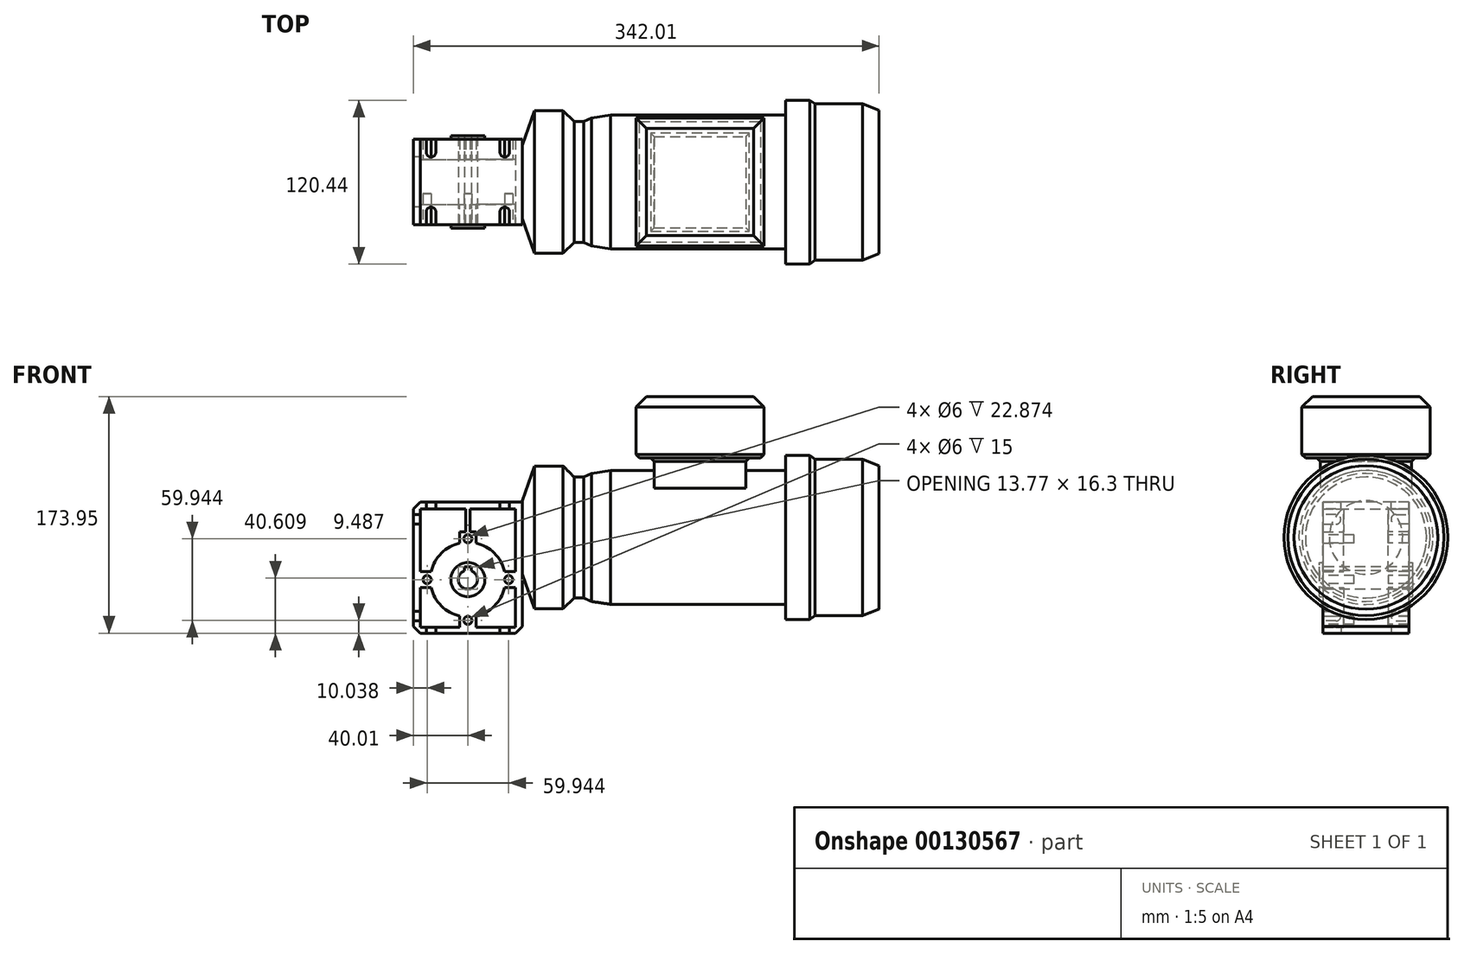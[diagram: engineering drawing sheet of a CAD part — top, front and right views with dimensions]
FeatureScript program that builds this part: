
annotation { "Feature Type Name" : "Feature", "Feature Type Description" : "" }
export const myFeature = defineFeature(function(context is Context, id is Id, definition is map)
    precondition{}
    {
        {
            var Q0;
            Q0=qCreatedBy(makeId("Top.planeOp"),FACE);
            var sketch = newSketch(context, id + "F0", { "sketchPlane" : qUnion([Q0])});
            skLineSegment(sketch, "E0.bottom", {"start": v(-40, 16.5) * mm, "end": v(40, 16.5) * mm});
            skLineSegment(sketch, "E0.top", {"start": v(-40, -16.5) * mm, "end": v(40, -16.5) * mm});
            skLineSegment(sketch, "E0.left", {"start": v(-40, 16.5) * mm, "end": v(-40, -16.5) * mm});
            skLineSegment(sketch, "E0.right", {"start": v(40, 16.5) * mm, "end": v(40, -16.5) * mm});
            skPoint(sketch, "E0.middle", {"position": v(0, 0) * mm});
            skSolve(sketch);
        }
        {
            var Q0;
            Q0=qSketchRegion(id+"F0",true);
            extrude(context, id + "F1", {"entities" : qUnion([Q0]), "endBound" : BoundingType.SYMMETRIC, "depth" : 96.35 * mm});
        }
        {
            var Q0;
            Q0=makeQuery(id+"F1.opExtrude","SWEPT_FACE",FACE,{"disambiguationData":[OSD([sQuery(id+"F0.wireOp",EDGE,"E0.top")])]});
            var sketch = newSketch(context, id + "F2", { "sketchPlane" : qUnion([Q0])});
            skArc(sketch, "E1", {"start": v(-2.5, -2.18) * mm, "mid": v(0, -15.72) * mm, "end": v(2.5, -2.18) * mm});
            skLineSegment(sketch, "E2", {"start": v(-2.5, -2.18) * mm, "end": v(-2.5, 0.58) * mm});
            skLineSegment(sketch, "E3", {"start": v(-2.5, 0.58) * mm, "end": v(2.5, 0.58) * mm});
            skLineSegment(sketch, "E4", {"start": v(2.5, 0.58) * mm, "end": v(2.5, -2.18) * mm});
            skPoint(sketch, "E5", {"position": v(0, -15.72) * mm});
            skSolve(sketch);
        }
        {
            var Q0;
            Q0=qSketchRegion(id+"F2",true);
            extrude(context, id + "F3", {"entities" : qUnion([Q0]), "operationType" : NewBodyOperationType.REMOVE, "endBound" : BoundingType.UP_TO_NEXT, "oppositeDirection" : true, "depth" : 25.4 * mm});
        }
        {
            var Q0;
            Q0=qCreatedBy(makeId("Front.planeOp"),FACE);
            var sketch = newSketch(context, id + "F4", { "sketchPlane" : qUnion([Q0])});
            skCircle(sketch, "E6", {"center": v(0, -8.72) * mm, "radius": 12.5 * mm});
            skArc(sketch, "E7.0", {"start": v(-2.5, -2.18) * mm, "mid": v(0, -15.72) * mm, "end": v(2.5, -2.18) * mm});
            skLineSegment(sketch, "E8.0", {"start": v(2.5, 0.58) * mm, "end": v(2.5, -2.18) * mm});
            skLineSegment(sketch, "E9.0", {"start": v(-2.5, 0.58) * mm, "end": v(2.5, 0.58) * mm});
            skLineSegment(sketch, "E10.0", {"start": v(-2.5, -2.18) * mm, "end": v(-2.5, 0.58) * mm});
            skSolve(sketch);
        }
        {
            var Q0;
            Q0=qSketchRegion(id+"F4",true);
            extrude(context, id + "F5", {"entities" : qUnion([Q0]), "operationType" : NewBodyOperationType.ADD, "endBound" : BoundingType.SYMMETRIC, "depth" : 68.07 * mm});
        }
        {
            var Q0;
            Q0=makeQuery(id+"F1.opExtrude","SWEPT_FACE",FACE,{"disambiguationData":[OSD([sQuery(id+"F0.wireOp",EDGE,"E0.top")])]});
            var sketch = newSketch(context, id + "F6", { "sketchPlane" : qUnion([Q0])});
            skCircle(sketch, "E11", {"center": v(0, 21.25) * mm, "radius": 3 * mm});
            skPoint(sketch, "E12", {"position": v(0, -8.72) * mm});
            skCircle(sketch, "E13.1.0", {"center": v(-29.97, -8.72) * mm, "radius": 3 * mm});
            skCircle(sketch, "E13.2.0", {"center": v(0, -38.7) * mm, "radius": 3 * mm});
            skCircle(sketch, "E13.3.0", {"center": v(29.97, -8.72) * mm, "radius": 3 * mm});
            skSolve(sketch);
        }
        {
            var Q0;
            Q0=qSketchRegion(id+"F6",true);
            extrude(context, id + "F7", {"entities" : qUnion([Q0]), "operationType" : NewBodyOperationType.REMOVE, "oppositeDirection" : true, "depth" : 7.87 * mm});
        }
        {
            var Q0;
            Q0=makeQuery(id+"F1.opExtrude","SWEPT_FACE",FACE,{"disambiguationData":[OSD([sQuery(id+"F0.wireOp",EDGE,"E0.top")])]});
            var sketch = newSketch(context, id + "F8", { "sketchPlane" : qUnion([Q0])});
            skLineSegment(sketch, "E14", {"start": v(-6, 18.12) * mm, "end": v(-6, 26.28) * mm});
            skLineSegment(sketch, "E15", {"start": v(-6, 26.28) * mm, "end": v(6, 26.28) * mm});
            skLineSegment(sketch, "E16", {"start": v(6, 26.28) * mm, "end": v(6, 18.12) * mm});
            skArc(sketch, "E17", {"start": v(-6, 18.12) * mm, "mid": v(-19.45, 10.72) * mm, "end": v(-26.84, -2.72) * mm});
            skArc(sketch, "E18", {"start": v(6, 18.12) * mm, "mid": v(0, 18.78) * mm, "end": v(-6, 18.12) * mm, "construction": true});
            skLineSegment(sketch, "E19", {"start": v(-6, -35.56) * mm, "end": v(-6, -35.56) * mm});
            skLineSegment(sketch, "E20", {"start": v(-6, -43.72) * mm, "end": v(6, -43.72) * mm});
            skLineSegment(sketch, "E21", {"start": v(6, -43.72) * mm, "end": v(6, -35.56) * mm});
            skLineSegment(sketch, "E22", {"start": v(-6, -35.56) * mm, "end": v(-6, -43.72) * mm});
            skArc(sketch, "E23", {"start": v(-6, -35.56) * mm, "mid": v(0, -36.22) * mm, "end": v(6, -35.56) * mm, "construction": true});
            skArc(sketch, "E24", {"start": v(6, -35.56) * mm, "mid": v(19.45, -28.17) * mm, "end": v(26.84, -14.72) * mm});
            skLineSegment(sketch, "E25", {"start": v(-35, -2.72) * mm, "end": v(-35, -14.72) * mm});
            skLineSegment(sketch, "E26", {"start": v(-35, -14.72) * mm, "end": v(-26.84, -14.72) * mm});
            skLineSegment(sketch, "E27", {"start": v(26.84, -2.72) * mm, "end": v(35, -2.72) * mm});
            skLineSegment(sketch, "E28", {"start": v(35, -2.72) * mm, "end": v(35, -14.72) * mm});
            skLineSegment(sketch, "E29", {"start": v(35, -14.72) * mm, "end": v(26.84, -14.72) * mm});
            skLineSegment(sketch, "E30", {"start": v(-35, -2.72) * mm, "end": v(-26.84, -2.72) * mm});
            skArc(sketch, "E31", {"start": v(-26.84, -2.72) * mm, "mid": v(-27.5, -8.72) * mm, "end": v(-26.84, -14.72) * mm, "construction": true});
            skArc(sketch, "E32", {"start": v(-26.84, -14.72) * mm, "mid": v(-19.45, -28.17) * mm, "end": v(-6, -35.56) * mm});
            skArc(sketch, "E33", {"start": v(26.84, -14.72) * mm, "mid": v(27.5, -8.72) * mm, "end": v(26.84, -2.72) * mm, "construction": true});
            skArc(sketch, "E34", {"start": v(26.84, -2.72) * mm, "mid": v(19.45, 10.72) * mm, "end": v(6, 18.12) * mm});
            skLineSegment(sketch, "E35", {"start": v(-35, -2.72) * mm, "end": v(-35, 43.17) * mm});
            skLineSegment(sketch, "E36", {"start": v(-35, 43.17) * mm, "end": v(-1.5, 43.17) * mm});
            skLineSegment(sketch, "E37", {"start": v(-1.5, 43.17) * mm, "end": v(-1.5, 26.28) * mm});
            skLineSegment(sketch, "E38", {"start": v(1.5, 26.28) * mm, "end": v(1.5, 43.17) * mm});
            skLineSegment(sketch, "E39", {"start": v(1.5, 43.17) * mm, "end": v(35, 43.17) * mm});
            skLineSegment(sketch, "E40", {"start": v(35, 43.17) * mm, "end": v(35, -2.72) * mm});
            skLineSegment(sketch, "E41", {"start": v(35, -14.72) * mm, "end": v(35, -43.72) * mm});
            skLineSegment(sketch, "E42", {"start": v(35, -43.72) * mm, "end": v(6, -43.72) * mm});
            skLineSegment(sketch, "E43", {"start": v(-35, -14.72) * mm, "end": v(-35, -43.72) * mm});
            skLineSegment(sketch, "E44", {"start": v(-35, -43.72) * mm, "end": v(-6, -43.72) * mm});
            skLineSegment(sketch, "E45", {"start": v(-35, 43.17) * mm, "end": v(-40, 43.17) * mm, "construction": true});
            skLineSegment(sketch, "E46", {"start": v(-35, 43.17) * mm, "end": v(-35, 48.17) * mm, "construction": true});
            skSolve(sketch);
        }
        {
            var Q0;
            Q0=makeQuery(id+"F8.imprint","IMPRINT",FACE,{"disambiguationData":[TD([[makeQuery(id+"F8.imprint","IMPRINT",EDGE,{"derivedFrom":sQuery(id+"F8.wireOp",EDGE,"E20")}),-1.0]])]});
            var Q1;
            {var subQ4=sQuery(id+"F8.wireOp",EDGE,"E14");Q1=makeQuery(id+"F8.imprint","IMPRINT",FACE,{"disambiguationData":[TD([[makeQuery(id+"F8.imprint","IMPRINT",EDGE,{"derivedFrom":subQ4}),-1.0]])]});}
            extrude(context, id + "F9", {"entities" : qUnion([Q0, Q1]), "depth" : 15 * mm});
        }
        {
            var Q0;
            Q0=makeQuery(id+"F9.opExtrude","SWEPT_BODY",BODY,{"disambiguationData":[OSD([sQuery(id+"F0.wireOp",EDGE,"E0.top"),sQuery(id+"F0.wireOp",EDGE,"E0.left"),sQuery(id+"F0.wireOp",EDGE,"E0.right"),sQuery(id+"F4.wireOp",EDGE,"E6"),sQuery(id+"F6.wireOp",EDGE,"E11"),sQuery(id+"F6.wireOp",EDGE,"E13.1.0"),sQuery(id+"F6.wireOp",EDGE,"E13.2.0"),sQuery(id+"F6.wireOp",EDGE,"E13.3.0"),sQuery(id+"F8.wireOp",EDGE,"E14"),sQuery(id+"F8.wireOp",EDGE,"E15"),sQuery(id+"F8.wireOp",EDGE,"E16"),sQuery(id+"F8.wireOp",EDGE,"E17"),sQuery(id+"F8.wireOp",EDGE,"E21"),sQuery(id+"F8.wireOp",EDGE,"E22"),sQuery(id+"F8.wireOp",EDGE,"E24"),sQuery(id+"F8.wireOp",EDGE,"E26"),sQuery(id+"F8.wireOp",EDGE,"E27"),sQuery(id+"F8.wireOp",EDGE,"E29"),sQuery(id+"F8.wireOp",EDGE,"E30"),sQuery(id+"F8.wireOp",EDGE,"E32"),sQuery(id+"F8.wireOp",EDGE,"E34"),sQuery(id+"F8.wireOp",EDGE,"E35"),sQuery(id+"F8.wireOp",EDGE,"E36"),sQuery(id+"F8.wireOp",EDGE,"E37"),sQuery(id+"F8.wireOp",EDGE,"E38"),sQuery(id+"F8.wireOp",EDGE,"E39"),sQuery(id+"F8.wireOp",EDGE,"E40"),sQuery(id+"F8.wireOp",EDGE,"E41"),sQuery(id+"F8.wireOp",EDGE,"E42"),sQuery(id+"F8.wireOp",EDGE,"E43"),sQuery(id+"F8.wireOp",EDGE,"E44")])]});
            var Q1;
            Q1=qCreatedBy(makeId("Front.planeOp"),FACE);
            mirror(context, id + "F10", {"operationType" : NewBodyOperationType.ADD, "entities" : qUnion([Q0]), "mirrorPlane" : qUnion([Q1])});
        }
        {
            var Q0;
            {var subQ0=sQuery(id+"F0.wireOp",EDGE,"E0.top");var subQ1=makeQuery(id+"F9.opExtrude","SWEPT_FACE",FACE,{"disambiguationData":[OSD([subQ0]),TDD([makeQuery(id+"F8.imprint","IMPRINT",EDGE,{"derivedFrom":makeQuery(id+"F1.opExtrude","CAP_EDGE",EDGE,{"disambiguationData":[OSD([subQ0])],"isStart":false})})])]});Q0=makeQuery(id+"F10.boolean.opBoolean","MERGE",FACE,{"derivedFrom":[makeQuery(id+"F1.opExtrude","CAP_FACE",FACE,{"disambiguationData":[OSD([sQuery(id+"F0.wireOp",EDGE,"E0.bottom"),subQ0,sQuery(id+"F0.wireOp",EDGE,"E0.left"),sQuery(id+"F0.wireOp",EDGE,"E0.right")])],"isStart":false}),subQ1,makeQuery(id+"F10.opPattern","COPY",FACE,{"derivedFrom":subQ1,"instanceName":"1"})]});}
            var sketch = newSketch(context, id + "F11", { "sketchPlane" : qUnion([Q0])});
            skLineSegment(sketch, "E47", {"start": v(-30.6, -31.5) * mm, "end": v(-30.6, -21.97) * mm});
            skLineSegment(sketch, "E48", {"start": v(-23.5, -31.5) * mm, "end": v(-23.5, -21.97) * mm});
            skArc(sketch, "E49", {"start": v(-30.6, -21.97) * mm, "mid": v(-27.05, -18.41) * mm, "end": v(-23.5, -21.97) * mm});
            skLineSegment(sketch, "E50", {"start": v(-30.6, -31.5) * mm, "end": v(-23.5, -31.5) * mm});
            skArc(sketch, "E51.MirrorCS", {"start": v(30.6, -21.97) * mm, "mid": v(27.05, -18.41) * mm, "end": v(23.5, -21.97) * mm});
            skLineSegment(sketch, "E52.MirrorCS", {"start": v(23.5, -31.5) * mm, "end": v(23.5, -21.97) * mm});
            skLineSegment(sketch, "E53.MirrorCS", {"start": v(30.6, -31.5) * mm, "end": v(30.6, -21.97) * mm});
            skLineSegment(sketch, "E54.MirrorCS", {"start": v(30.6, -31.5) * mm, "end": v(23.5, -31.5) * mm});
            skArc(sketch, "E55.MirrorCS", {"start": v(-30.6, 21.97) * mm, "mid": v(-27.05, 18.41) * mm, "end": v(-23.5, 21.97) * mm});
            skLineSegment(sketch, "E56.MirrorCS", {"start": v(-30.6, 31.5) * mm, "end": v(-30.6, 21.97) * mm});
            skLineSegment(sketch, "E57.MirrorCS", {"start": v(-23.5, 31.5) * mm, "end": v(-23.5, 21.97) * mm});
            skLineSegment(sketch, "E58.MirrorCS", {"start": v(-30.6, 31.5) * mm, "end": v(-23.5, 31.5) * mm});
            skLineSegment(sketch, "E59.MirrorCS", {"start": v(30.6, 31.5) * mm, "end": v(23.5, 31.5) * mm});
            skLineSegment(sketch, "E60.MirrorCS", {"start": v(23.5, 31.5) * mm, "end": v(23.5, 21.97) * mm});
            skArc(sketch, "E61.MirrorCS", {"start": v(30.6, 21.97) * mm, "mid": v(27.05, 18.41) * mm, "end": v(23.5, 21.97) * mm});
            skLineSegment(sketch, "E62.MirrorCS", {"start": v(30.6, 31.5) * mm, "end": v(30.6, 21.97) * mm});
            skSolve(sketch);
        }
        {
            var Q0;
            Q0=qSketchRegion(id+"F11",true);
            extrude(context, id + "F12", {"entities" : qUnion([Q0]), "operationType" : NewBodyOperationType.REMOVE, "endBound" : BoundingType.UP_TO_NEXT, "oppositeDirection" : true, "depth" : 114.3 * mm});
        }
        {
            var Q0;
            {var subQ0=sQuery(id+"F0.wireOp",EDGE,"E0.top");var subQ1=makeQuery(id+"F9.opExtrude","SWEPT_FACE",FACE,{"disambiguationData":[OSD([subQ0]),TDD([makeQuery(id+"F8.imprint","IMPRINT",EDGE,{"derivedFrom":makeQuery(id+"F1.opExtrude","CAP_EDGE",EDGE,{"disambiguationData":[OSD([subQ0])],"isStart":true})})])]});Q0=makeQuery(id+"F10.boolean.opBoolean","MERGE",FACE,{"derivedFrom":[makeQuery(id+"F1.opExtrude","CAP_FACE",FACE,{"disambiguationData":[OSD([sQuery(id+"F0.wireOp",EDGE,"E0.bottom"),subQ0,sQuery(id+"F0.wireOp",EDGE,"E0.left"),sQuery(id+"F0.wireOp",EDGE,"E0.right")])],"isStart":true}),subQ1,makeQuery(id+"F10.opPattern","COPY",FACE,{"derivedFrom":subQ1,"instanceName":"1"})]});}
            var sketch = newSketch(context, id + "F13", { "sketchPlane" : qUnion([Q0])});
            skLineSegment(sketch, "E63.0", {"start": v(-23.5, 21.97) * mm, "end": v(-23.5, 31.5) * mm});
            skArc(sketch, "E64.0", {"start": v(-23.5, 21.97) * mm, "mid": v(-27.05, 18.41) * mm, "end": v(-30.6, 21.97) * mm});
            skLineSegment(sketch, "E65.0", {"start": v(-30.6, 21.97) * mm, "end": v(-30.6, 31.5) * mm});
            skLineSegment(sketch, "E66.0", {"start": v(23.5, 21.97) * mm, "end": v(23.5, 31.5) * mm});
            skArc(sketch, "E67.0", {"start": v(23.5, 21.97) * mm, "mid": v(27.05, 18.41) * mm, "end": v(30.6, 21.97) * mm});
            skLineSegment(sketch, "E68.0", {"start": v(30.6, 21.97) * mm, "end": v(30.6, 31.5) * mm});
            skLineSegment(sketch, "E69", {"start": v(-30.6, 31.5) * mm, "end": v(-23.5, 31.5) * mm});
            skLineSegment(sketch, "E70", {"start": v(23.5, 31.5) * mm, "end": v(30.6, 31.5) * mm});
            skLineSegment(sketch, "E71.MirrorCS", {"start": v(23.5, -21.97) * mm, "end": v(23.5, -31.5) * mm});
            skArc(sketch, "E72.MirrorCS", {"start": v(23.5, -21.97) * mm, "mid": v(27.05, -18.41) * mm, "end": v(30.6, -21.97) * mm});
            skLineSegment(sketch, "E73.MirrorCS", {"start": v(30.6, -21.97) * mm, "end": v(30.6, -31.5) * mm});
            skLineSegment(sketch, "E74.MirrorCS", {"start": v(23.5, -31.5) * mm, "end": v(30.6, -31.5) * mm});
            skLineSegment(sketch, "E75.MirrorCS", {"start": v(-30.6, -31.5) * mm, "end": v(-23.5, -31.5) * mm});
            skLineSegment(sketch, "E76.MirrorCS", {"start": v(-30.6, -21.97) * mm, "end": v(-30.6, -31.5) * mm});
            skArc(sketch, "E77.MirrorCS", {"start": v(-23.5, -21.97) * mm, "mid": v(-27.05, -18.41) * mm, "end": v(-30.6, -21.97) * mm});
            skLineSegment(sketch, "E78.MirrorCS", {"start": v(-23.5, -21.97) * mm, "end": v(-23.5, -31.5) * mm});
            skSolve(sketch);
        }
        {
            var Q0;
            Q0=qSketchRegion(id+"F13",true);
            extrude(context, id + "F14", {"entities" : qUnion([Q0]), "operationType" : NewBodyOperationType.REMOVE, "endBound" : BoundingType.UP_TO_NEXT, "oppositeDirection" : true, "depth" : 25.4 * mm});
        }
        {
            var Q0;
            {var subQ0=sQuery(id+"F0.wireOp",EDGE,"E0.left");var subQ1=makeQuery(id+"F9.opExtrude","SWEPT_FACE",FACE,{"disambiguationData":[OSD([sQuery(id+"F0.wireOp",EDGE,"E0.top"),subQ0])]});Q0=makeQuery(id+"F10.boolean.opBoolean","MERGE",FACE,{"derivedFrom":[makeQuery(id+"F1.opExtrude","SWEPT_FACE",FACE,{"disambiguationData":[OSD([subQ0])]}),subQ1,makeQuery(id+"F10.opPattern","COPY",FACE,{"derivedFrom":subQ1,"instanceName":"1"})]});}
            var sketch = newSketch(context, id + "F15", { "sketchPlane" : qUnion([Q0])});
            skLineSegment(sketch, "E79", {"start": v(31.5, 39.12) * mm, "end": v(31.5, 32) * mm});
            skArc(sketch, "E80.MirrorCS", {"start": v(21.97, 39.12) * mm, "mid": v(18.42, 35.56) * mm, "end": v(21.97, 32) * mm});
            skLineSegment(sketch, "E81", {"start": v(21.97, 39.12) * mm, "end": v(31.5, 39.12) * mm});
            skLineSegment(sketch, "E82", {"start": v(31.5, 32) * mm, "end": v(21.97, 32) * mm});
            skArc(sketch, "E83.MirrorCS", {"start": v(-21.97, 39.12) * mm, "mid": v(-18.41, 35.56) * mm, "end": v(-21.97, 32) * mm});
            skLineSegment(sketch, "E84.MirrorCS", {"start": v(-21.97, 39.12) * mm, "end": v(-31.5, 39.12) * mm});
            skLineSegment(sketch, "E85.MirrorCS", {"start": v(-31.5, 32) * mm, "end": v(-21.97, 32) * mm});
            skLineSegment(sketch, "E86.MirrorCS", {"start": v(-31.5, 39.12) * mm, "end": v(-31.5, 32) * mm});
            skLineSegment(sketch, "E87.MirrorCS", {"start": v(-31.5, -39.12) * mm, "end": v(-31.5, -32) * mm});
            skLineSegment(sketch, "E88.MirrorCS", {"start": v(-31.5, -32) * mm, "end": v(-21.97, -32) * mm});
            skArc(sketch, "E89.MirrorCS", {"start": v(-21.97, -39.12) * mm, "mid": v(-18.41, -35.56) * mm, "end": v(-21.97, -32) * mm});
            skLineSegment(sketch, "E90.MirrorCS", {"start": v(-21.97, -39.12) * mm, "end": v(-31.5, -39.12) * mm});
            skArc(sketch, "E91.MirrorCS", {"start": v(21.97, -39.12) * mm, "mid": v(18.42, -35.56) * mm, "end": v(21.97, -32) * mm});
            skLineSegment(sketch, "E92.MirrorCS", {"start": v(31.5, -32) * mm, "end": v(21.97, -32) * mm});
            skLineSegment(sketch, "E93.MirrorCS", {"start": v(31.5, -39.12) * mm, "end": v(31.5, -32) * mm});
            skLineSegment(sketch, "E94.MirrorCS", {"start": v(21.97, -39.12) * mm, "end": v(31.5, -39.12) * mm});
            skSolve(sketch);
        }
        {
            var Q0;
            Q0=qSketchRegion(id+"F15",true);
            extrude(context, id + "F16", {"entities" : qUnion([Q0]), "operationType" : NewBodyOperationType.REMOVE, "endBound" : BoundingType.UP_TO_NEXT, "oppositeDirection" : true, "depth" : 25.4 * mm});
        }
        {
            var Q0;
            {var subQ0=sQuery(id+"F0.wireOp",EDGE,"E0.right");var subQ1=makeQuery(id+"F9.opExtrude","SWEPT_FACE",FACE,{"disambiguationData":[OSD([sQuery(id+"F0.wireOp",EDGE,"E0.top"),subQ0])]});Q0=makeQuery(id+"F10.boolean.opBoolean","MERGE",FACE,{"derivedFrom":[makeQuery(id+"F1.opExtrude","SWEPT_FACE",FACE,{"disambiguationData":[OSD([subQ0])]}),subQ1,makeQuery(id+"F10.opPattern","COPY",FACE,{"derivedFrom":subQ1,"instanceName":"1"})]});}
            var sketch = newSketch(context, id + "F17", { "sketchPlane" : qUnion([Q0])});
            skLineSegment(sketch, "E95.0", {"start": v(-8.62, -11.72) * mm, "end": v(-8.62, -5.72) * mm, "construction": true});
            skPoint(sketch, "E96", {"position": v(-8.62, -8.72) * mm});
            skCircle(sketch, "E97", {"center": v(0, 22.27) * mm, "radius": 27 * mm});
            skSolve(sketch);
        }
        {
            var Q0;
            {var subQ0=sQuery(id+"F0.wireOp",EDGE,"E0.left");var subQ1=makeQuery(id+"F9.opExtrude","SWEPT_FACE",FACE,{"disambiguationData":[OSD([sQuery(id+"F0.wireOp",EDGE,"E0.top"),subQ0])]});Q0=makeQuery(id+"F10.boolean.opBoolean","MERGE",FACE,{"derivedFrom":[makeQuery(id+"F1.opExtrude","SWEPT_FACE",FACE,{"disambiguationData":[OSD([subQ0])]}),subQ1,makeQuery(id+"F10.opPattern","COPY",FACE,{"derivedFrom":subQ1,"instanceName":"1"})]});}
            cPlane(context, id + "F18", {"entities" : qUnion([Q0]), "cplaneType" : CPlaneType.OFFSET, "offset" : 89 * mm, "oppositeDirection" : true, "width" : 152.4 * mm, "height" : 152.4 * mm});
        }
        {
            var Q0;
            Q0=qCreatedBy(id+"F18.planeOp",FACE);
            var sketch = newSketch(context, id + "F19", { "sketchPlane" : qUnion([Q0])});
            skCircle(sketch, "E98", {"center": v(0, 22.27) * mm, "radius": 52.45 * mm});
            skSolve(sketch);
        }
        {
            var Q1;
            Q1=qSketchRegion(id+"F17",true);
            var Q2;
            Q2=qSketchRegion(id+"F19",true);
            loft(context, id + "F20", {"operationType" : NewBodyOperationType.ADD, "sheetProfilesArray" : [{ "sheetProfileEntities" : qUnion([Q1]) }, { "sheetProfileEntities" : qUnion([Q2]) }]});
        }
        {
            var Q0;
            Q0=qSketchRegion(id+"F19",true);
            extrude(context, id + "F21", {"entities" : qUnion([Q0]), "operationType" : NewBodyOperationType.ADD, "oppositeDirection" : true, "depth" : 21 * mm});
        }
        {
            var Q0;
            Q0=makeQuery(id+"F21.opExtrude","CAP_FACE",FACE,{"disambiguationData":[OSD([sQuery(id+"F19.wireOp",EDGE,"E98")])],"isStart":false});
            cPlane(context, id + "F22", {"entities" : qUnion([Q0]), "cplaneType" : CPlaneType.OFFSET, "offset" : 8 * mm, "width" : 152.4 * mm, "height" : 152.4 * mm});
        }
        {
            var Q0;
            Q0=qCreatedBy(id+"F22.planeOp",FACE);
            var sketch = newSketch(context, id + "F23", { "sketchPlane" : qUnion([Q0])});
            skCircle(sketch, "E99", {"center": v(0, 22.27) * mm, "radius": 44.45 * mm});
            skSolve(sketch);
        }
        {
            var Q1;
            Q1=makeQuery(id+"F21.opExtrude","CAP_FACE",FACE,{"disambiguationData":[OSD([sQuery(id+"F19.wireOp",EDGE,"E98")])],"isStart":false});
            var Q2;
            Q2=makeQuery(id+"F23.imprint","IMPRINT",FACE,{"disambiguationData":[TD([[makeQuery(id+"F23.imprint","IMPRINT",EDGE,{"derivedFrom":sQuery(id+"F23.wireOp",EDGE,"E99")}),1.0]])]});
            loft(context, id + "F24", {"operationType" : NewBodyOperationType.ADD, "sheetProfilesArray" : [{ "sheetProfileEntities" : qUnion([Q1]) }, { "sheetProfileEntities" : qUnion([Q2]) }]});
        }
        {
            var Q0;
            Q0=qCreatedBy(makeId("Front.planeOp"),FACE);
            var sketch = newSketch(context, id + "F25", { "sketchPlane" : qUnion([Q0])});
            skLineSegment(sketch, "E100.0", {"start": v(78, 66.72) * mm, "end": v(78, -22.18) * mm, "construction": true});
            skPoint(sketch, "E101", {"position": v(78, 22.27) * mm});
            skLineSegment(sketch, "E102", {"start": v(78, 66.72) * mm, "end": v(84.97, 66.72) * mm});
            skLineSegment(sketch, "E103", {"start": v(84.97, 66.72) * mm, "end": v(90.65, 69.3) * mm});
            skLineSegment(sketch, "E104", {"start": v(90.65, 69.3) * mm, "end": v(104.92, 71.49) * mm});
            skLineSegment(sketch, "E105", {"start": v(104.92, 71.49) * mm, "end": v(233.25, 71.49) * mm});
            skLineSegment(sketch, "E106", {"start": v(233.25, 71.49) * mm, "end": v(233.25, 82.49) * mm});
            skLineSegment(sketch, "E107", {"start": v(233.25, 82.49) * mm, "end": v(251.25, 82.49) * mm});
            skLineSegment(sketch, "E108", {"start": v(251.25, 82.49) * mm, "end": v(255, 79.65) * mm});
            skLineSegment(sketch, "E109", {"start": v(255, 79.65) * mm, "end": v(290, 79.65) * mm});
            skLineSegment(sketch, "E110", {"start": v(290, 79.65) * mm, "end": v(302, 75.05) * mm});
            skLineSegment(sketch, "E111", {"start": v(302, 75.05) * mm, "end": v(302, 22.27) * mm});
            skLineSegment(sketch, "E112", {"start": v(302, 22.27) * mm, "end": v(78, 22.27) * mm});
            skLineSegment(sketch, "E113", {"start": v(78, 66.72) * mm, "end": v(78, 22.27) * mm});
            skSolve(sketch);
        }
        {
            var Q0;
            Q0=makeQuery(id+"F25.imprint","IMPRINT",FACE,{"disambiguationData":[TD([[makeQuery(id+"F25.imprint","IMPRINT",EDGE,{"derivedFrom":sQuery(id+"F25.wireOp",EDGE,"E102")}),-1.0]])]});
            var Q1;
            Q1=sQuery(id+"F25.wireOp",EDGE,"E112");
            revolve(context, id + "F26", {"operationType" : NewBodyOperationType.ADD, "entities" : qUnion([Q0]), "axis" : qUnion([Q1]), "revolveType" : RevolveType.FULL});
        }
        {
            var Q0;
            Q0=qCreatedBy(makeId("Top.planeOp"),FACE);
            var sketch = newSketch(context, id + "F27", { "sketchPlane" : qUnion([Q0])});
            skLineSegment(sketch, "E114.bottom", {"start": v(204, 33.5) * mm, "end": v(137, 33.5) * mm});
            skLineSegment(sketch, "E114.top", {"start": v(204, -33.5) * mm, "end": v(137, -33.5) * mm});
            skLineSegment(sketch, "E114.left", {"start": v(204, 33.5) * mm, "end": v(204, -33.5) * mm});
            skLineSegment(sketch, "E114.right", {"start": v(137, 33.5) * mm, "end": v(137, -33.5) * mm});
            skPoint(sketch, "E114.middle", {"position": v(170.5, 0) * mm});
            skSolve(sketch);
        }
        {
            var Q0;
            Q0=qSketchRegion(id+"F27",true);
            extrude(context, id + "F28", {"entities" : qUnion([Q0]), "operationType" : NewBodyOperationType.ADD, "depth" : 80.77 * mm});
        }
        {
            var Q0;
            Q0=makeQuery(id+"F28.opExtrude","CAP_FACE",FACE,{"disambiguationData":[OSD([sQuery(id+"F27.wireOp",EDGE,"E114.bottom"),sQuery(id+"F27.wireOp",EDGE,"E114.top"),sQuery(id+"F27.wireOp",EDGE,"E114.left"),sQuery(id+"F27.wireOp",EDGE,"E114.right")])],"isStart":false});
            var sketch = newSketch(context, id + "F29", { "sketchPlane" : qUnion([Q0])});
            skLineSegment(sketch, "E115.bottom", {"start": v(123.5, 47) * mm, "end": v(217.5, 47) * mm});
            skLineSegment(sketch, "E115.top", {"start": v(123.5, -47) * mm, "end": v(217.5, -47) * mm});
            skLineSegment(sketch, "E115.left", {"start": v(123.5, 47) * mm, "end": v(123.5, -47) * mm});
            skLineSegment(sketch, "E115.right", {"start": v(217.5, 47) * mm, "end": v(217.5, -47) * mm});
            skPoint(sketch, "E115.middle", {"position": v(170.5, 0) * mm});
            skPoint(sketch, "E116", {"position": v(170.5, 33.5) * mm});
            skPoint(sketch, "E117", {"position": v(170.5, 47) * mm});
            skSolve(sketch);
        }
        {
            var Q0;
            Q0=qSketchRegion(id+"F29",true);
            extrude(context, id + "F30", {"entities" : qUnion([Q0]), "operationType" : NewBodyOperationType.ADD, "depth" : 45 * mm});
        }
        {
            var Q0;
            Q0=makeQuery(id+"F30.opExtrude","CAP_FACE",FACE,{"disambiguationData":[OSD([sQuery(id+"F29.wireOp",EDGE,"E115.bottom"),sQuery(id+"F29.wireOp",EDGE,"E115.top"),sQuery(id+"F29.wireOp",EDGE,"E115.left"),sQuery(id+"F29.wireOp",EDGE,"E115.right")])],"isStart":false});
            chamfer(context, id + "F31", {"entities" : qUnion([Q0]), "width" : 7.62 * mm, "tangentPropagation" : true});
        }
        {
            var Q0;
            Q0=makeQuery(id+"F30.opExtrude","CAP_FACE",FACE,{"disambiguationData":[OSD([sQuery(id+"F29.wireOp",EDGE,"E115.bottom"),sQuery(id+"F29.wireOp",EDGE,"E115.top"),sQuery(id+"F29.wireOp",EDGE,"E115.left"),sQuery(id+"F29.wireOp",EDGE,"E115.right")])],"isStart":true});
            chamfer(context, id + "F32", {"entities" : qUnion([Q0]), "width" : 2.54 * mm, "tangentPropagation" : true});
        }
        {
            var Q0;
            {var subQ0=sQuery(id+"F0.wireOp",EDGE,"E0.top");var subQ1=sQuery(id+"F0.wireOp",EDGE,"E0.left");var subQ2=makeQuery(id+"F9.opExtrude","SWEPT_EDGE",EDGE,{"disambiguationData":[OSD([subQ0,subQ1]),TDD([makeQuery(id+"F8.imprint","INTERSECT",VERTEX,{"derivedFrom":[makeQuery(id+"F1.opExtrude","SWEPT_EDGE",EDGE,{"disambiguationData":[OSD([subQ0,subQ1])]}),makeQuery(id+"F1.opExtrude","CAP_EDGE",EDGE,{"disambiguationData":[OSD([subQ0])],"isStart":false})]})])]});Q0=makeQuery(id+"F10.boolean.opBoolean","MERGE",EDGE,{"derivedFrom":[makeQuery(id+"F1.opExtrude","CAP_EDGE",EDGE,{"disambiguationData":[OSD([subQ1])],"isStart":false}),subQ2,makeQuery(id+"F10.opPattern","COPY",EDGE,{"derivedFrom":subQ2,"instanceName":"1"})]});}
            var Q1;
            {var subQ0=sQuery(id+"F0.wireOp",EDGE,"E0.top");var subQ1=sQuery(id+"F0.wireOp",EDGE,"E0.left");var subQ2=makeQuery(id+"F9.opExtrude","SWEPT_EDGE",EDGE,{"disambiguationData":[OSD([subQ0,subQ1]),TDD([makeQuery(id+"F8.imprint","INTERSECT",VERTEX,{"derivedFrom":[makeQuery(id+"F1.opExtrude","SWEPT_EDGE",EDGE,{"disambiguationData":[OSD([subQ0,subQ1])]}),makeQuery(id+"F1.opExtrude","CAP_EDGE",EDGE,{"disambiguationData":[OSD([subQ0])],"isStart":true})]})])]});Q1=makeQuery(id+"F10.boolean.opBoolean","MERGE",EDGE,{"derivedFrom":[makeQuery(id+"F1.opExtrude","CAP_EDGE",EDGE,{"disambiguationData":[OSD([subQ1])],"isStart":true}),subQ2,makeQuery(id+"F10.opPattern","COPY",EDGE,{"derivedFrom":subQ2,"instanceName":"1"})]});}
            var Q2;
            {var subQ0=sQuery(id+"F0.wireOp",EDGE,"E0.top");var subQ1=sQuery(id+"F0.wireOp",EDGE,"E0.right");var subQ2=makeQuery(id+"F9.opExtrude","SWEPT_EDGE",EDGE,{"disambiguationData":[OSD([subQ0,subQ1]),TDD([makeQuery(id+"F8.imprint","INTERSECT",VERTEX,{"derivedFrom":[makeQuery(id+"F1.opExtrude","SWEPT_EDGE",EDGE,{"disambiguationData":[OSD([subQ0,subQ1])]}),makeQuery(id+"F1.opExtrude","CAP_EDGE",EDGE,{"disambiguationData":[OSD([subQ0])],"isStart":true})]})])]});Q2=makeQuery(id+"F10.boolean.opBoolean","MERGE",EDGE,{"derivedFrom":[makeQuery(id+"F1.opExtrude","CAP_EDGE",EDGE,{"disambiguationData":[OSD([subQ1])],"isStart":true}),subQ2,makeQuery(id+"F10.opPattern","COPY",EDGE,{"derivedFrom":subQ2,"instanceName":"1"})]});}
            chamfer(context, id + "F33", {"entities" : qUnion([Q0, Q1, Q2]), "width" : 5.08 * mm, "tangentPropagation" : true});
        }
    });
